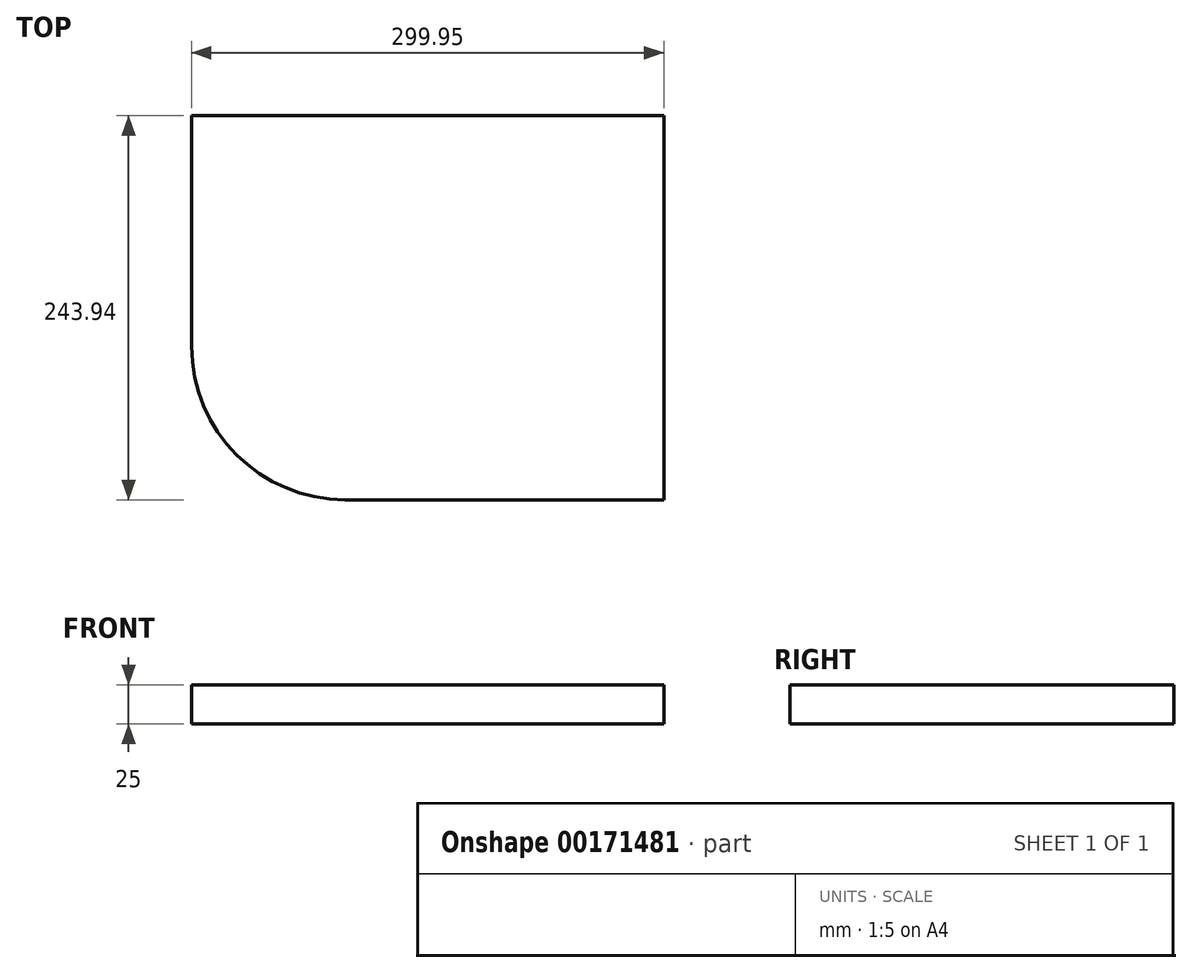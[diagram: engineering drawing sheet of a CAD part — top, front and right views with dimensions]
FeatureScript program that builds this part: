
annotation { "Feature Type Name" : "Feature", "Feature Type Description" : "" }
export const myFeature = defineFeature(function(context is Context, id is Id, definition is map)
    precondition{}
    {
        {
            var Q0;
            Q0=qCreatedBy(makeId("Top.planeOp"),FACE);
            var sketch = newSketch(context, id + "F0", { "sketchPlane" : qUnion([Q0])});
            skLineSegment(sketch, "E0.bottom", {"start": v(146.81, -121.97) * mm, "end": v(-153.14, -121.97) * mm});
            skLineSegment(sketch, "E0.top", {"start": v(146.81, 121.97) * mm, "end": v(-153.14, 121.97) * mm});
            skLineSegment(sketch, "E0.left", {"start": v(146.81, -121.97) * mm, "end": v(146.81, 121.97) * mm});
            skLineSegment(sketch, "E0.right", {"start": v(-153.14, -121.97) * mm, "end": v(-153.14, 121.97) * mm});
            skPoint(sketch, "E0.middle", {"position": v(-3.17, 0) * mm});
            skSolve(sketch);
        }
        {
            var Q0;
            Q0 = qSketchRegion(id + "F0", true);
            extrude(context, id + "F1", {"entities" : qUnion([Q0]), "depth" : 25 * mm});
        }
        {
            var Q0;
            Q0=makeQuery(id+"F1.opExtrude","SWEPT_EDGE",EDGE,{"disambiguationData":[OSD([sQuery(id+"F0.wireOp",EDGE,"E0.bottom"),sQuery(id+"F0.wireOp",EDGE,"E0.right")])]});
            fillet(context, id + "F2", {"entities" : qUnion([Q0]), "radius" : 97.53 * mm, "tangentPropagation" : true, "allowEdgeOverflow" : false});
        }
    });
